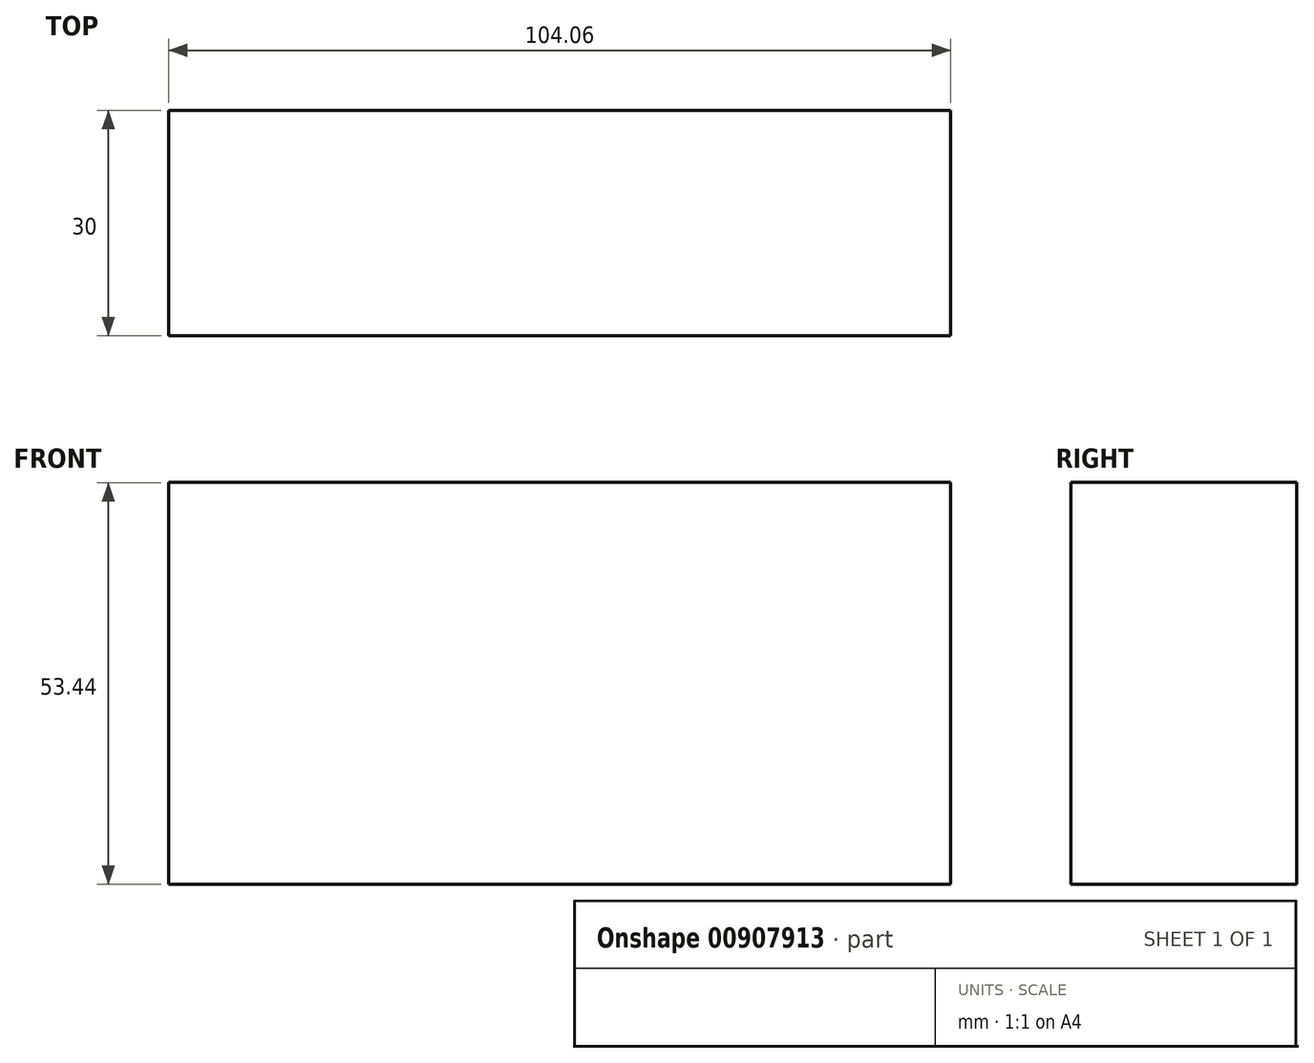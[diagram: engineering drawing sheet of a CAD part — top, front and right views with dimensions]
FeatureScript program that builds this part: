
annotation { "Feature Type Name" : "Feature", "Feature Type Description" : "" }
export const myFeature = defineFeature(function(context is Context, id is Id, definition is map)
    precondition{}
    {
        {
            var Q0;
            Q0=qCreatedBy(makeId("Front.planeOp"),FACE);
            var sketch = newSketch(context, id + "F0", { "sketchPlane" : qUnion([Q0])});
            skLineSegment(sketch, "E0.bottom", {"start": v(-52.03, -26.72) * mm, "end": v(52.03, -26.72) * mm});
            skLineSegment(sketch, "E0.top", {"start": v(-52.03, 26.72) * mm, "end": v(52.03, 26.72) * mm});
            skLineSegment(sketch, "E0.left", {"start": v(-52.03, -26.72) * mm, "end": v(-52.03, 26.72) * mm});
            skLineSegment(sketch, "E0.right", {"start": v(52.03, -26.72) * mm, "end": v(52.03, 26.72) * mm});
            skPoint(sketch, "E0.middle", {"position": v(0, 0) * mm});
            skSolve(sketch);
        }
        {
            var Q0;
            Q0=makeQuery(id+"F0.imprint","IMPRINT",FACE,{"disambiguationData":[TD([[makeQuery(id+"F0.imprint","IMPRINT",EDGE,{"derivedFrom":sQuery(id+"F0.wireOp",EDGE,"E0.bottom")}),1.0]])]});
            extrude(context, id + "F1", {"entities" : qUnion([Q0]), "depth" : 30 * mm, "offsetDistance" : 25.4 * mm});
        }
    });
